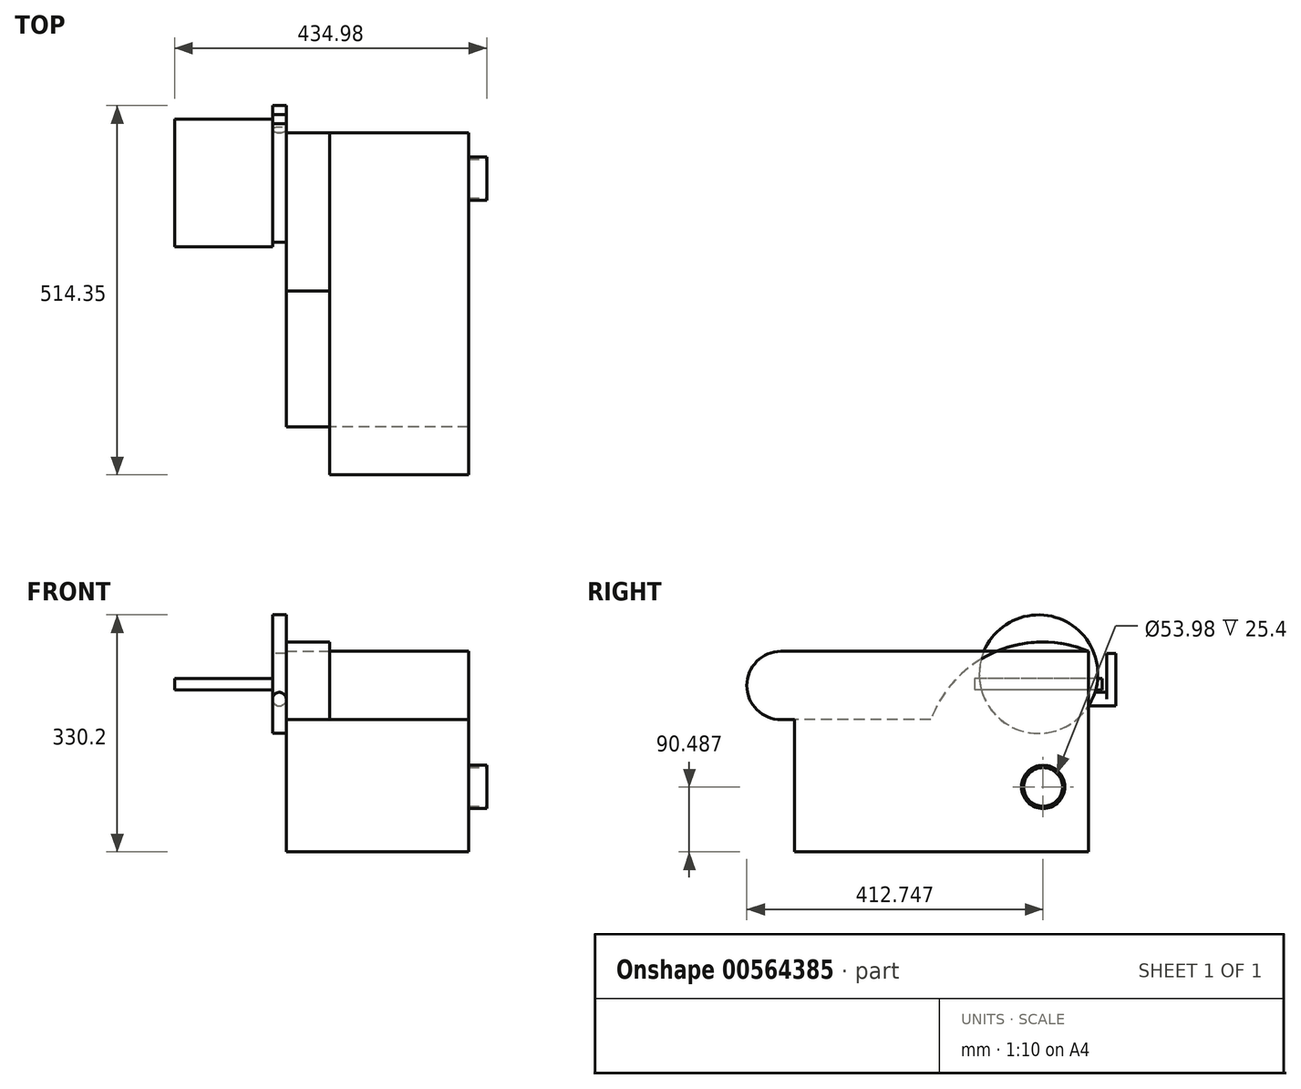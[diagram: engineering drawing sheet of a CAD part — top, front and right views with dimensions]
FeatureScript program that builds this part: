
annotation { "Feature Type Name" : "Feature", "Feature Type Description" : "" }
export const myFeature = defineFeature(function(context is Context, id is Id, definition is map)
    precondition{}
    {
        {
            var Q0;
            Q0=qCreatedBy(makeId("Top.planeOp"),FACE);
            var sketch = newSketch(context, id + "F0", { "sketchPlane" : qUnion([Q0])});
            skLineSegment(sketch, "E0.bottom", {"start": v(127, 204.79) * mm, "end": v(-127, 204.79) * mm});
            skLineSegment(sketch, "E0.top", {"start": v(127, -204.79) * mm, "end": v(-127, -204.79) * mm});
            skLineSegment(sketch, "E0.left", {"start": v(127, 204.79) * mm, "end": v(127, -204.79) * mm});
            skLineSegment(sketch, "E0.right", {"start": v(-127, 204.79) * mm, "end": v(-127, -204.79) * mm});
            skPoint(sketch, "E0.middle", {"position": v(0, 0) * mm});
            skSolve(sketch);
        }
        {
            var Q0;
            Q0 = qSketchRegion(id + "F0", true);
            extrude(context, id + "F1", {"entities" : qUnion([Q0]), "depth" : 184.15 * mm, "offsetDistance" : 25.4 * mm});
        }
        {
            var Q0;
            Q0=makeQuery(id+"F1.opExtrude","CAP_FACE",FACE,{"disambiguationData":[OSD([sQuery(id+"F0.wireOp",EDGE,"E0.bottom"),sQuery(id+"F0.wireOp",EDGE,"E0.top"),sQuery(id+"F0.wireOp",EDGE,"E0.left"),sQuery(id+"F0.wireOp",EDGE,"E0.right")])],"isStart":false});
            var sketch = newSketch(context, id + "F2", { "sketchPlane" : qUnion([Q0])});
            skLineSegment(sketch, "E1.bottom", {"start": v(127, 204.79) * mm, "end": v(-66.67, 204.79) * mm});
            skLineSegment(sketch, "E1.top", {"start": v(127, -271.46) * mm, "end": v(-66.67, -271.46) * mm});
            skLineSegment(sketch, "E1.left", {"start": v(127, 204.79) * mm, "end": v(127, -271.46) * mm});
            skLineSegment(sketch, "E1.right", {"start": v(-66.67, 204.79) * mm, "end": v(-66.67, -271.46) * mm});
            skSolve(sketch);
        }
        {
            var Q0;
            Q0 = qSketchRegion(id + "F2", true);
            extrude(context, id + "F3", {"entities" : qUnion([Q0]), "operationType" : NewBodyOperationType.ADD, "depth" : 95.25 * mm, "offsetDistance" : 25.4 * mm});
        }
        {
            var Q0;
            Q0=makeQuery(id+"F3.boolean.opBoolean","MERGE",FACE,{"derivedFrom":[makeQuery(id+"F1.opExtrude","SWEPT_FACE",FACE,{"disambiguationData":[OSD([sQuery(id+"F0.wireOp",EDGE,"E0.left")])]}),makeQuery(id+"F3.opExtrude","SWEPT_FACE",FACE,{"disambiguationData":[OSD([sQuery(id+"F2.wireOp",EDGE,"E1.left")])]})]});
            var sketch = newSketch(context, id + "F4", { "sketchPlane" : qUnion([Q0])});
            skSolve(sketch);
        }
        {
            var Q0;
            {var subQ1=sQuery(id+"F0.wireOp",EDGE,"E0.left");Q0=makeQuery(id+"F4.imprint","IMPRINT",FACE,{"disambiguationData":[TD([[makeQuery(id+"F4.imprint","IMPRINT",EDGE,{"derivedFrom":makeQuery(id+"F1.opExtrude","CAP_EDGE",EDGE,{"disambiguationData":[OSD([subQ1])],"isStart":true})}),-1.0]])]});}
            var sketch = newSketch(context, id + "F5", { "sketchPlane" : qUnion([Q0])});
            skCircle(sketch, "E2", {"center": v(141.29, 90.49) * mm, "radius": 30.16 * mm});
            skSolve(sketch);
        }
        {
            var Q0;
            Q0 = qSketchRegion(id + "F5", true);
            extrude(context, id + "F6", {"entities" : qUnion([Q0]), "operationType" : NewBodyOperationType.ADD, "depth" : 25.4 * mm, "offsetDistance" : 25.4 * mm});
        }
        {
            var Q0;
            Q0=makeQuery(id+"F6.opExtrude","CAP_FACE",FACE,{"disambiguationData":[OSD([sQuery(id+"F5.wireOp",EDGE,"E2")])],"isStart":false});
            var sketch = newSketch(context, id + "F7", { "sketchPlane" : qUnion([Q0])});
            skCircle(sketch, "E3.0", {"center": v(141.29, 90.49) * mm, "radius": 26.99 * mm});
            skSolve(sketch);
        }
        {
            var Q0;
            Q0 = qSketchRegion(id + "F7", true);
            extrude(context, id + "F8", {"entities" : qUnion([Q0]), "operationType" : NewBodyOperationType.REMOVE, "oppositeDirection" : true, "depth" : 25.4 * mm, "offsetDistance" : 25.4 * mm});
        }
        {
            var Q0;
            Q0=makeQuery(id+"F1.opExtrude","SWEPT_FACE",FACE,{"disambiguationData":[OSD([sQuery(id+"F0.wireOp",EDGE,"E0.right")])]});
            var sketch = newSketch(context, id + "F9", { "sketchPlane" : qUnion([Q0])});
            skCircle(sketch, "E4", {"center": v(-134.94, 247.65) * mm, "radius": 82.55 * mm});
            skSolve(sketch);
        }
        {
            var Q0;
            Q0 = qSketchRegion(id + "F9", true);
            extrude(context, id + "F10", {"entities" : qUnion([Q0]), "operationType" : NewBodyOperationType.ADD, "depth" : 19.05 * mm, "offsetDistance" : 25.4 * mm});
        }
        {
            var Q0;
            Q0=makeQuery(id+"F10.opExtrude","CAP_FACE",FACE,{"disambiguationData":[OSD([sQuery(id+"F9.wireOp",EDGE,"E4")])],"isStart":false});
            var sketch = newSketch(context, id + "F11", { "sketchPlane" : qUnion([Q0])});
            skLineSegment(sketch, "E5.bottom", {"start": v(-223.84, 241.3) * mm, "end": v(-46.04, 241.3) * mm});
            skLineSegment(sketch, "E5.top", {"start": v(-223.84, 225.43) * mm, "end": v(-46.04, 225.43) * mm});
            skLineSegment(sketch, "E5.left", {"start": v(-223.84, 241.3) * mm, "end": v(-223.84, 225.43) * mm});
            skLineSegment(sketch, "E5.right", {"start": v(-46.04, 241.3) * mm, "end": v(-46.04, 225.43) * mm});
            skLineSegment(sketch, "E6", {"start": v(-134.94, 247.65) * mm, "end": v(-134.94, 165.1) * mm, "construction": true});
            skLineSegment(sketch, "E7", {"start": v(-134.94, 241.3) * mm, "end": v(-134.94, 225.43) * mm, "construction": true});
            skSolve(sketch);
        }
        {
            var Q0;
            Q0 = qSketchRegion(id + "F11", true);
            extrude(context, id + "F12", {"entities" : qUnion([Q0]), "operationType" : NewBodyOperationType.ADD, "depth" : 136.53 * mm, "offsetDistance" : 25.4 * mm});
        }
        {
            var Q0;
            Q0=makeQuery(id+"F3.opExtrude","SWEPT_FACE",FACE,{"disambiguationData":[OSD([sQuery(id+"F2.wireOp",EDGE,"E1.right")])]});
            var sketch = newSketch(context, id + "F13", { "sketchPlane" : qUnion([Q0])});
            skLineSegment(sketch, "E8.top", {"start": v(-204.79, 184.15) * mm, "end": v(15.27, 184.15) * mm});
            skLineSegment(sketch, "E8.left", {"start": v(-204.79, 279.4) * mm, "end": v(-204.79, 184.15) * mm});
            skArc(sketch, "E9", {"start": v(15.27, 184.15) * mm, "mid": v(-74.48, 278.62) * mm, "end": v(-204.79, 279.4) * mm});
            skSolve(sketch);
        }
        {
            var Q0;
            Q0 = qSketchRegion(id + "F13", true);
            var Q1;
            Q1=makeQuery(id+"F10.opExtrude","CAP_FACE",FACE,{"disambiguationData":[OSD([sQuery(id+"F9.wireOp",EDGE,"E4")])],"isStart":true});
            extrude(context, id + "F14", {"entities" : qUnion([Q0]), "operationType" : NewBodyOperationType.ADD, "endBound" : BoundingType.UP_TO_SURFACE, "depth" : 25.4 * mm, "endBoundEntityFace" : qUnion([Q1]), "offsetDistance" : 25.4 * mm});
        }
        {
            var Q0;
            Q0=makeQuery(id+"F3.opExtrude","SWEPT_FACE",FACE,{"disambiguationData":[OSD([sQuery(id+"F2.wireOp",EDGE,"E1.right")])]});
            var sketch = newSketch(context, id + "F15", { "sketchPlane" : qUnion([Q0])});
            skArc(sketch, "E10", {"start": v(223.84, 184.15) * mm, "mid": v(271.46, 231.78) * mm, "end": v(223.84, 279.4) * mm});
            skLineSegment(sketch, "E11", {"start": v(223.84, 279.4) * mm, "end": v(271.46, 279.4) * mm});
            skLineSegment(sketch, "E12", {"start": v(271.46, 279.4) * mm, "end": v(271.46, 184.15) * mm});
            skLineSegment(sketch, "E13", {"start": v(271.46, 184.15) * mm, "end": v(223.84, 184.15) * mm});
            skSolve(sketch);
        }
        {
            var Q0;
            Q0 = qSketchRegion(id + "F15", true);
            var Q1;
            Q1=makeQuery(id+"F3.boolean.opBoolean","MERGE",FACE,{"derivedFrom":[makeQuery(id+"F1.opExtrude","SWEPT_FACE",FACE,{"disambiguationData":[OSD([sQuery(id+"F0.wireOp",EDGE,"E0.left")])]}),makeQuery(id+"F3.opExtrude","SWEPT_FACE",FACE,{"disambiguationData":[OSD([sQuery(id+"F2.wireOp",EDGE,"E1.left")])]})]});
            extrude(context, id + "F16", {"entities" : qUnion([Q0]), "operationType" : NewBodyOperationType.REMOVE, "endBound" : BoundingType.UP_TO_SURFACE, "oppositeDirection" : true, "depth" : 25.4 * mm, "endBoundEntityFace" : qUnion([Q1]), "offsetDistance" : 25.4 * mm});
        }
        {
            var Q0;
            Q0=makeQuery(id+"F14.boolean.opBoolean","MERGE",FACE,{"derivedFrom":[makeQuery(id+"F3.boolean.opBoolean","MERGE",FACE,{"derivedFrom":[makeQuery(id+"F1.opExtrude","SWEPT_FACE",FACE,{"disambiguationData":[OSD([sQuery(id+"F0.wireOp",EDGE,"E0.bottom")])]}),makeQuery(id+"F3.opExtrude","SWEPT_FACE",FACE,{"disambiguationData":[OSD([sQuery(id+"F2.wireOp",EDGE,"E1.bottom")])]})]}),makeQuery(id+"F14.opExtrude","SWEPT_FACE",FACE,{"disambiguationData":[OSD([sQuery(id+"F13.wireOp",EDGE,"E8.left")])]})]});
            var sketch = newSketch(context, id + "F17", { "sketchPlane" : qUnion([Q0])});
            skCircle(sketch, "E14", {"center": v(136.52, 212.73) * mm, "radius": 9.53 * mm});
            skSolve(sketch);
        }
        {
            var Q0;
            Q0 = qSketchRegion(id + "F17", true);
            extrude(context, id + "F18", {"entities" : qUnion([Q0]), "operationType" : NewBodyOperationType.ADD, "depth" : 38.1 * mm, "offsetDistance" : 25.4 * mm});
        }
        {
            var Q0;
            Q0=makeQuery(id+"F18.opExtrude","CAP_FACE",FACE,{"disambiguationData":[OSD([sQuery(id+"F17.wireOp",EDGE,"E14")])],"isStart":false});
            var sketch = newSketch(context, id + "F19", { "sketchPlane" : qUnion([Q0])});
            skLineSegment(sketch, "E15.bottom", {"start": v(127, 212.73) * mm, "end": v(146.05, 212.73) * mm});
            skLineSegment(sketch, "E15.top", {"start": v(127, 276.23) * mm, "end": v(146.05, 276.23) * mm});
            skLineSegment(sketch, "E15.left", {"start": v(127, 212.73) * mm, "end": v(127, 276.23) * mm});
            skLineSegment(sketch, "E15.right", {"start": v(146.05, 212.73) * mm, "end": v(146.05, 276.23) * mm});
            skSolve(sketch);
        }
        {
            var Q0;
            Q0 = qSketchRegion(id + "F19", true);
            extrude(context, id + "F20", {"entities" : qUnion([Q0]), "operationType" : NewBodyOperationType.ADD, "oppositeDirection" : true, "depth" : 12.7 * mm, "offsetDistance" : 25.4 * mm});
        }
    });
